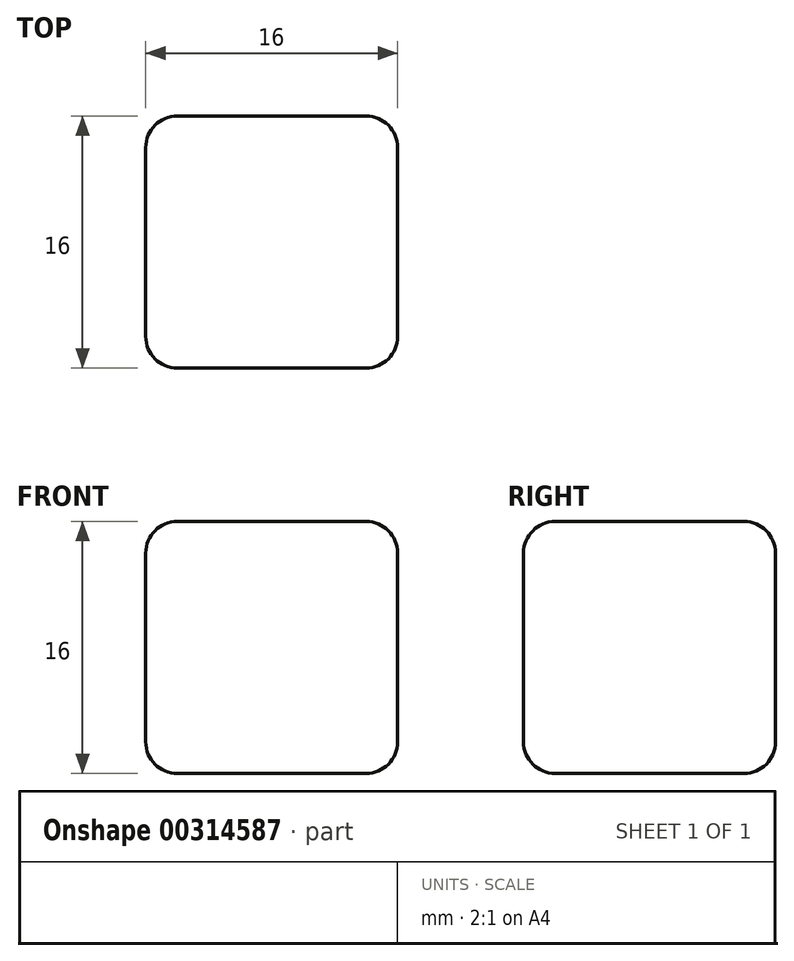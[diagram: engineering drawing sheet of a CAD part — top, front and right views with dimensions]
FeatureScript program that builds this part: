
annotation { "Feature Type Name" : "Feature", "Feature Type Description" : "" }
export const myFeature = defineFeature(function(context is Context, id is Id, definition is map)
    precondition{}
    {
        {
            var Q0;
            Q0=qCreatedBy(makeId("Front.planeOp"),FACE);
            var sketch = newSketch(context, id + "F0", { "sketchPlane" : qUnion([Q0])});
            skLineSegment(sketch, "E0.bottom", {"start": v(8, 8) * mm, "end": v(-8, 8) * mm});
            skLineSegment(sketch, "E0.top", {"start": v(8, -8) * mm, "end": v(-8, -8) * mm});
            skLineSegment(sketch, "E0.left", {"start": v(8, 8) * mm, "end": v(8, -8) * mm});
            skLineSegment(sketch, "E0.right", {"start": v(-8, 8) * mm, "end": v(-8, -8) * mm});
            skPoint(sketch, "E0.middle", {"position": v(0, 0) * mm});
            skSolve(sketch);
        }
        {
            var Q0;
            Q0 = qSketchRegion(id + "F0", true);
            extrude(context, id + "F1", {"entities" : qUnion([Q0]), "depth" : 16 * mm});
        }
        {
            var Q0;
            Q0=makeQuery(id+"F1.opExtrude","CAP_EDGE",EDGE,{"disambiguationData":[OSD([sQuery(id+"F0.wireOp",EDGE,"E0.bottom")])],"isStart":false});
            var Q1;
            Q1=makeQuery(id+"F1.opExtrude","SWEPT_EDGE",EDGE,{"disambiguationData":[OSD([sQuery(id+"F0.wireOp",EDGE,"E0.bottom"),sQuery(id+"F0.wireOp",EDGE,"E0.left")])]});
            var Q2;
            Q2=makeQuery(id+"F1.opExtrude","SWEPT_EDGE",EDGE,{"disambiguationData":[OSD([sQuery(id+"F0.wireOp",EDGE,"E0.top"),sQuery(id+"F0.wireOp",EDGE,"E0.left")])]});
            var Q3;
            Q3=makeQuery(id+"F1.opExtrude","CAP_EDGE",EDGE,{"disambiguationData":[OSD([sQuery(id+"F0.wireOp",EDGE,"E0.right")])],"isStart":false});
            var Q4;
            Q4=makeQuery(id+"F1.opExtrude","CAP_EDGE",EDGE,{"disambiguationData":[OSD([sQuery(id+"F0.wireOp",EDGE,"E0.left")])],"isStart":true});
            var Q5;
            Q5=makeQuery(id+"F1.opExtrude","CAP_EDGE",EDGE,{"disambiguationData":[OSD([sQuery(id+"F0.wireOp",EDGE,"E0.left")])],"isStart":false});
            var Q6;
            Q6=makeQuery(id+"F1.opExtrude","SWEPT_EDGE",EDGE,{"disambiguationData":[OSD([sQuery(id+"F0.wireOp",EDGE,"E0.top"),sQuery(id+"F0.wireOp",EDGE,"E0.right")])]});
            var Q7;
            Q7=makeQuery(id+"F1.opExtrude","SWEPT_EDGE",EDGE,{"disambiguationData":[OSD([sQuery(id+"F0.wireOp",EDGE,"E0.bottom"),sQuery(id+"F0.wireOp",EDGE,"E0.right")])]});
            var Q8;
            Q8=makeQuery(id+"F1.opExtrude","CAP_EDGE",EDGE,{"disambiguationData":[OSD([sQuery(id+"F0.wireOp",EDGE,"E0.right")])],"isStart":true});
            var Q9;
            Q9=makeQuery(id+"F1.opExtrude","CAP_EDGE",EDGE,{"disambiguationData":[OSD([sQuery(id+"F0.wireOp",EDGE,"E0.bottom")])],"isStart":true});
            var Q10;
            Q10=makeQuery(id+"F1.opExtrude","CAP_EDGE",EDGE,{"disambiguationData":[OSD([sQuery(id+"F0.wireOp",EDGE,"E0.top")])],"isStart":true});
            fillet(context, id + "F2", {"entities" : qUnion([Q0, Q1, Q2, Q3, Q4, Q5, Q6, Q7, Q8, Q9, Q10]), "radius" : 2 * mm, "tangentPropagation" : true, "allowEdgeOverflow" : false});
        }
        {
            var Q0;
            Q0=makeQuery(id+"F1.opExtrude","CAP_EDGE",EDGE,{"disambiguationData":[OSD([sQuery(id+"F0.wireOp",EDGE,"E0.top")])],"isStart":false});
            fillet(context, id + "F3", {"entities" : qUnion([Q0]), "radius" : 2 * mm, "tangentPropagation" : true, "allowEdgeOverflow" : false});
        }
    });
